# Revit family: PRD_FrankeWS_PprTwlDspnsrs_RODANPaperTowelDispenser_RODX600TT
name_source: partatom
category: Specialty Equipment
revit_build: Autodesk Revit 2018 (Build: 20190510_1515(x64)
units: mm (PartAtom-declared; Revit-internal decimal feet)

## family parameters
Cut with Voids When Loaded = Yes
Host = Face
OmniClass Number = 23.40.20.21.17
OmniClass Title = Paper Towel Dispensers, Disposal Units
Part Type = Normal
Room Calculation Point = No
Round Connector Dimension = Use Diameter
Shared = No

## types (1)
- RODX600TT
    AssetType = Fixed
    BIMObjectName = PRD_AR_PaperTowelDispensers_RODANPaperTowelDispenser_RODX600TT
    Category = Pr_40_70_22_62, Paper Towel Dispensers
    Default Elevation = 850 mm  [stored 2.78871 ft]
    Description = Paper towel dispenser for installation from the front or from the top, stainless steel, surfaces satin finished, material strength 1 mm, capacity for 600 pieces of C-folded single-layer paper towels. Can be filled from the top.
    DispenserMaterial = PRD_AR_StainlessSteel_SatinFinished
    DurationUnit = year
    Features = stainless steel, surface satin finished
    FillingQuantity = 600
    FillingQuantityUom = Towels
    Finish = satin finished
    GrossWeight = 5.00 kg
    IfcExportAs = IfcFurnitureType
    IfcExportType = USERDEFINED
    IsBuiltIn = TRUE
    Lock = No lock
    MainColor = stainless steel
    Manufacturer = KWC Group AG
    ManufacturerName = KWC Group AG
    ManufacturerURL = www.kwc.com
    Material = stainless steel
    MaterialCode = 1.4301
    MaterialThickness = 1.00 mm
    Model = RODX600TT
    ModelNumber = 2000102672
    ModelReference = RODX600TT
    NBSDescription = Paper towel dispensers
    NBSReference = 45-35-72/344
    Name = Paper Towel Dispenser RODX600TT
    NetWeight = 4.20 kg
    NominalDepth = 180 mm  [stored 0.590551 ft]
    NominalHeight = 445 mm  [stored 1.45997 ft]
    NominalWidth = 330 mm  [stored 1.08268 ft]
    Offset = 0 mm  [stored 0 ft]
    ProductInformation = https://pim.kwc.com
    Size = 330 x 445 x 180 mm
    Style = Dispenser
    TypeOfConsumable = Paper towel
    TypeOfFixing = Glue
    TypeOfMounting = Counter top mounting
    TypeOfOperation = Manual operation
    URL = www.kwc.com
    Uniclass2015Code = Pr_40_70_22_62
    Uniclass2015Title = Paper towel dispensers
    Uniclass2015Version = Products v1.17
    Version = 1
    WarrantyDurationUnit = year

note: [stored X ft] marks values corroborated as IEEE doubles in the binary element streams (Revit-internal decimal feet)

## geometry (parser evidence)
native form markers: Sweep x2
no freeform markers — native parametric forms only
